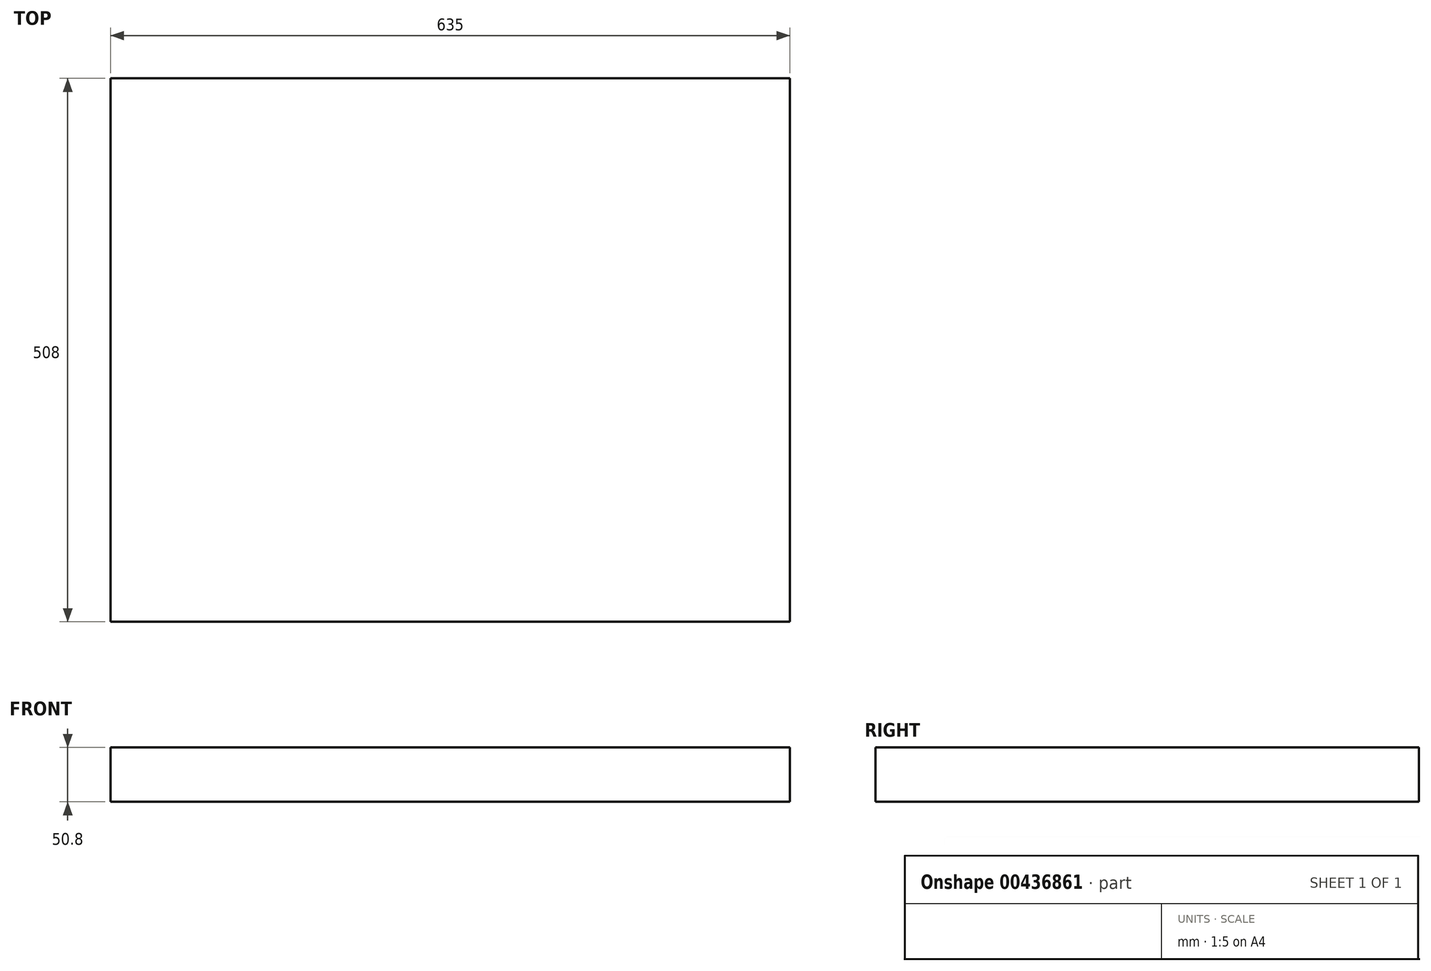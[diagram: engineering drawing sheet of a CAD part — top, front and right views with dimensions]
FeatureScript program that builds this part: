
annotation { "Feature Type Name" : "Feature", "Feature Type Description" : "" }
export const myFeature = defineFeature(function(context is Context, id is Id, definition is map)
    precondition{}
    {
        {
            var Q0;
            Q0=qCreatedBy(makeId("Top.planeOp"),FACE);
            var sketch = newSketch(context, id + "F0", { "sketchPlane" : qUnion([Q0])});
            skLineSegment(sketch, "E0.bottom", {"start": v(-317.5, 254) * mm, "end": v(317.5, 254) * mm});
            skLineSegment(sketch, "E0.top", {"start": v(-317.5, -254) * mm, "end": v(317.5, -254) * mm});
            skLineSegment(sketch, "E0.left", {"start": v(-317.5, 254) * mm, "end": v(-317.5, -254) * mm});
            skLineSegment(sketch, "E0.right", {"start": v(317.5, 254) * mm, "end": v(317.5, -254) * mm});
            skSolve(sketch);
        }
        {
            var Q0;
            Q0 = qSketchRegion(id + "F0", true);
            extrude(context, id + "F1", {"entities" : qUnion([Q0]), "depth" : 50.8 * mm});
        }
    });
